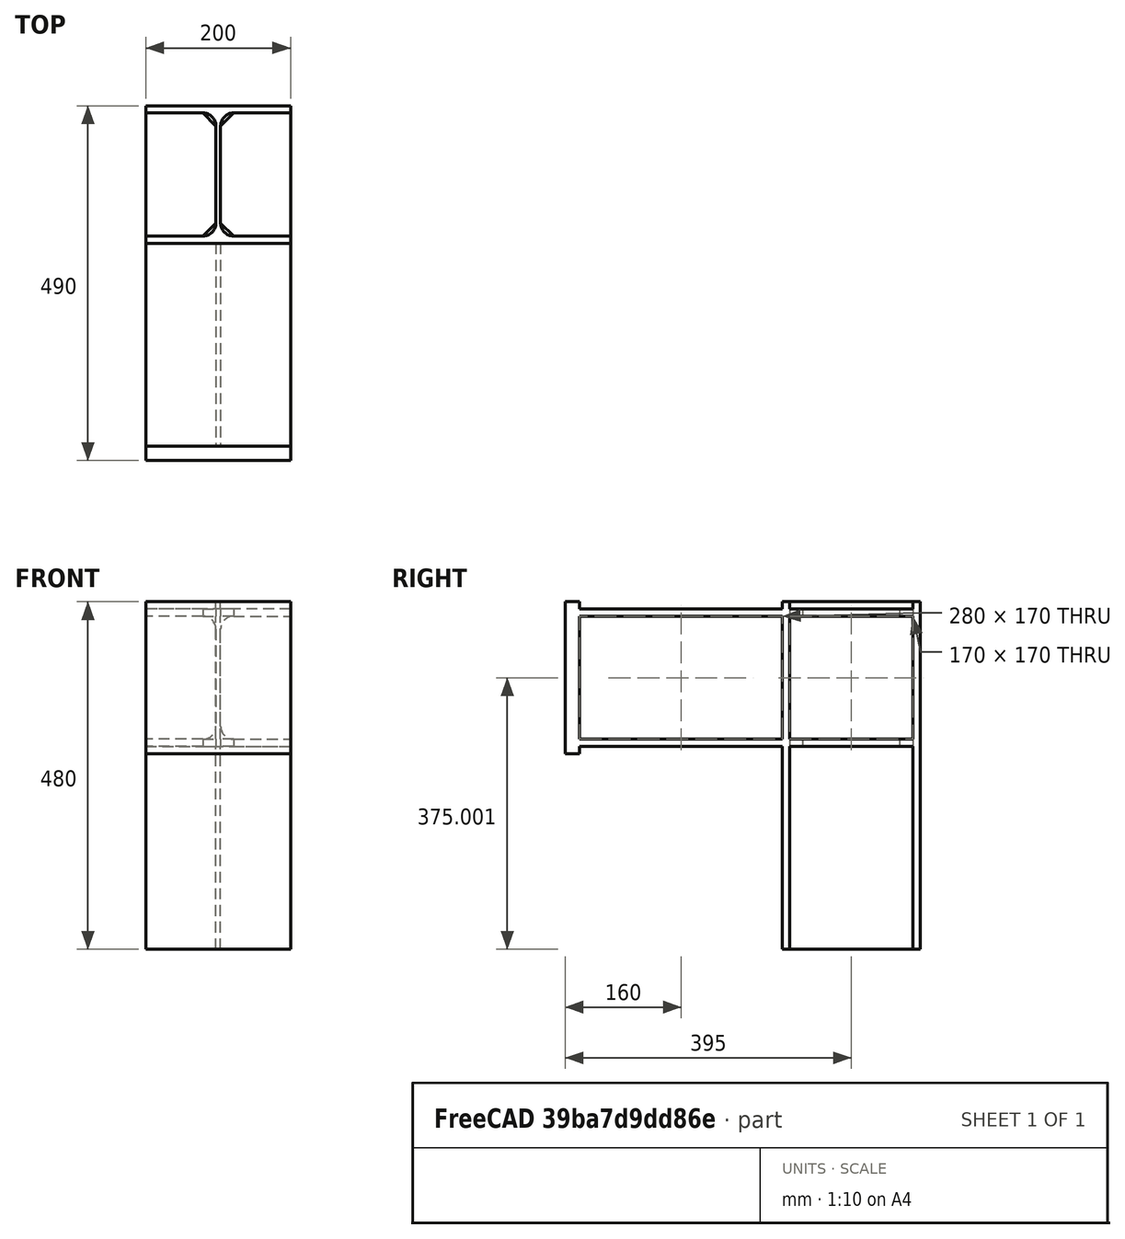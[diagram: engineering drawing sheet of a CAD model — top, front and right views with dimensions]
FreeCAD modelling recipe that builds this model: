
FCSTD DOCUMENT  (FreeCAD 0.21R33694 (Git))
Label: HEA200_frame_corner
License: All rights reserved
LicenseURL: http://en.wikipedia.org/wiki/All_rights_reserved
objects: Fem::ConstraintForce×2, Part::Feature×1, Sketcher::SketchObject×1, Part::Extrusion×1, Part::MultiFuse×1, App::MaterialObjectPython×1, Fem::ConstraintFixed×1, Fem::FemSolverObjectPython×1, Fem::FemMeshObjectPython×1, Fem::FemAnalysis×1
note: 4 computed .brp shape members not serialized (recipe doc carries the construction recipe); baked Part::Feature solids carry a one-line shape summary decoded from their .brp

FEATURE [Part::Feature] Fusion003012  label="corner"
  shape: bbox 200 x 470 x 480 mm, 60 faces (baked)
FEATURE [Sketcher::SketchObject] Sketch
  ExternalGeometry = -> [Fusion003012]
  FullyConstrained = true
  MapMode = 5
  Placement = pos=(0,5070,0) rot=(1,0,0;1.5708rad)
  Support = -> [Fusion003012]
  sketch-geometry (4):
    g0: LineSegment StartX=336.75 StartY=7245.73 StartZ=0 EndX=536.75 EndY=7245.73 EndZ=0
    g1: LineSegment StartX=536.75 StartY=7245.73 StartZ=0 EndX=536.75 EndY=7035.73 EndZ=0
    g2: LineSegment StartX=536.75 StartY=7035.73 StartZ=0 EndX=336.75 EndY=7035.73 EndZ=0
    g3: LineSegment StartX=336.75 StartY=7035.73 StartZ=0 EndX=336.75 EndY=7245.73 EndZ=0
  constraints (12):
    c: Coincident(g0,g1)
    c: Coincident(g1,g2)
    c: Coincident(g2,g3)
    c: Coincident(g3,g0)
    c: Horizontal(g0)
    c: Horizontal(g2)
    c: Vertical(g1)
    c: Vertical(g3)
    c: Vertical(g0,g-3)
    c: Vertical(g-3,g0)
    c: DistanceY(g-3,g0) = 10
    c: DistanceY(g1,g-4) = 10
FEATURE [Part::Extrusion] Extrude
  Base = -> Sketch
  Dir = (0,-1,2e-16)
  DirMode = 2
  FaceMakerClass = Part::FaceMakerBullseye
  LengthFwd = 20
  LengthRev = 0
  Solid = true
  Symmetric = false
FEATURE [Part::MultiFuse] Fusion
  Refine = true
  Shapes = -> [Fusion003012,Extrude]
FEATURE [App::MaterialObjectPython] MaterialSolid  label="S235"  # material (typed FeaturePython)
  Category = 0
  Material = AuthorAndLicense=(c) 2013 Juergen Riegel (CC-BY 3.0),CardName=CalculiX-Steel,Density=7900 kg/m^3,+8 more (map truncated)
FEATURE [Fem::ConstraintFixed] ConstraintFixed
  NormalDirection = (0,0,-1)
  Normals = (8) [(0,0,-1),(0,0,-1),(0,0,-1),(0,0,-1),(0,0,-1),(0,0,-1),(0,0,-1),(0,0,-1)]
  Points = (8) [(336.75,5350,6765.73),(403.417,5350,6765.73),(470.084,5350,6765.73),(536.75,5350,6765.73),(336.75,5540,6765.73),(403.417,5540,6765.73),+2 more]
  References = -> [Fusion]
  Scale = 15
FEATURE [Fem::ConstraintForce] ConstraintForce
  Direction = -> Fusion [Edge39]
  DirectionVector = (0,-1,0)
  Force = 119000
  NormalDirection = (0,2e-16,1)
  Points = (12) [(336.75,5050,7245.73),(403.417,5050,7245.73),(470.084,5050,7245.73),(536.75,5050,7245.73),(336.75,5060,7245.73),(403.417,5060,7245.73),+6 more]
  References = -> [Fusion]
  Scale = 10
FEATURE [Fem::ConstraintForce] ConstraintForce001
  Direction = -> Fusion [Edge43]
  DirectionVector = (0,1,0)
  Force = 119000
  NormalDirection = (0,-2e-16,-1)
  Points = (12) [(536.75,5050,7035.73),(470.084,5050,7035.73),(403.417,5050,7035.73),(336.75,5050,7035.73),(536.75,5060,7035.73),(470.084,5060,7035.73),+6 more]
  References = -> [Fusion]
  Reversed = true
  Scale = 10
FEATURE [Fem::FemSolverObjectPython] SolverCcxTools  # FEM object (typed FeaturePython)
  AnalysisType = 0
  BeamShellResultOutput3D = true
  BucklingFactors = 1
  EigenmodeHighLimit = 1000000
  EigenmodeLowLimit = 0
  EigenmodesCount = 10
  GeometricalNonlinearity = 0
  IterationsControlParameterCutb = 0.25,0.5,0.75,0.85,,,1.5,
  IterationsControlParameterIter = 4,8,9,200,10,400,,200,,
  IterationsControlParameterTimeUse = false
  IterationsThermoMechMaximum = 2000
  IterationsUserDefinedIncrementations = false
  IterationsUserDefinedTimeStepLength = false
  MaterialNonlinearity = 0
  MatrixSolverType = 1
  SplitInputWriter = true
  ThermoMechSteadyState = true
  TimeEnd = 1
  TimeInitialStep = 0.01
FEATURE [Fem::FemMeshObjectPython] FEMMeshGmsh  # FEM object (typed FeaturePython)
  Algorithm2D = 0
  Algorithm3D = 0
  CharacteristicLengthMax = 10
  CharacteristicLengthMin = 0
  CoherenceMesh = true
  ElementDimension = 0
  ElementOrder = 1
  GeometryTolerance = 1e-06
  GroupsOfNodes = false
  HighOrderOptimize = 0
  MeshSizeFromCurvature = 12
  OptimizeNetgen = false
  OptimizeStd = true
  Part = -> Fusion
  RecombinationAlgorithm = 0
  Recombine3DAll = false
  RecombineAll = false
  SecondOrderLinear = false
FEATURE [Fem::FemAnalysis] Analysis
  Group = -> [MaterialSolid,ConstraintFixed,ConstraintForce,ConstraintForce001,SolverCcxTools,FEMMeshGmsh]
